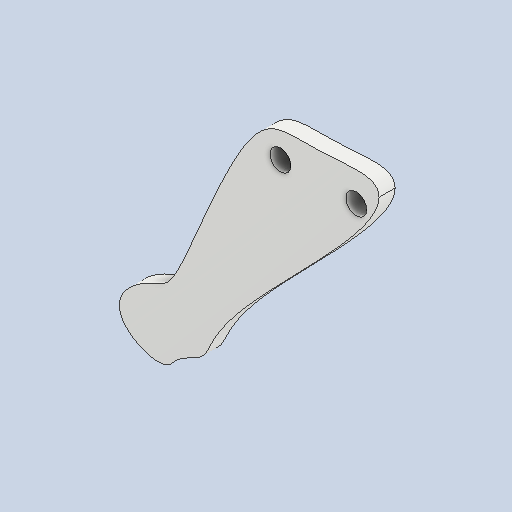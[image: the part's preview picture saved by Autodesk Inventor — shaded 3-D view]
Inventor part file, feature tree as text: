
AUTODESK INVENTOR PART (.ipt)
format: ipt  version: 2022 (Build 260153000, 153)  size: 108,032 bytes
history: native  units: in
note: dims shown in document units (in); Inventor stores cm internally (conversion verified against a paired STEP export)
features: other x3, sketch x1
ambient origin geometry x8: Origin, YZ Plane, XZ Plane, XY Plane, X Axis, Y Axis, Z Axis, Center Point
bodies: Solid1 (feature_tree)
feature tree (4):
  other  "Component30.ipt"
  other  "Solid1::Component30.ipt"
  other  "TaggingFeature1"
  sketch  "Sketch2"  dims[d0=0.3937in]
